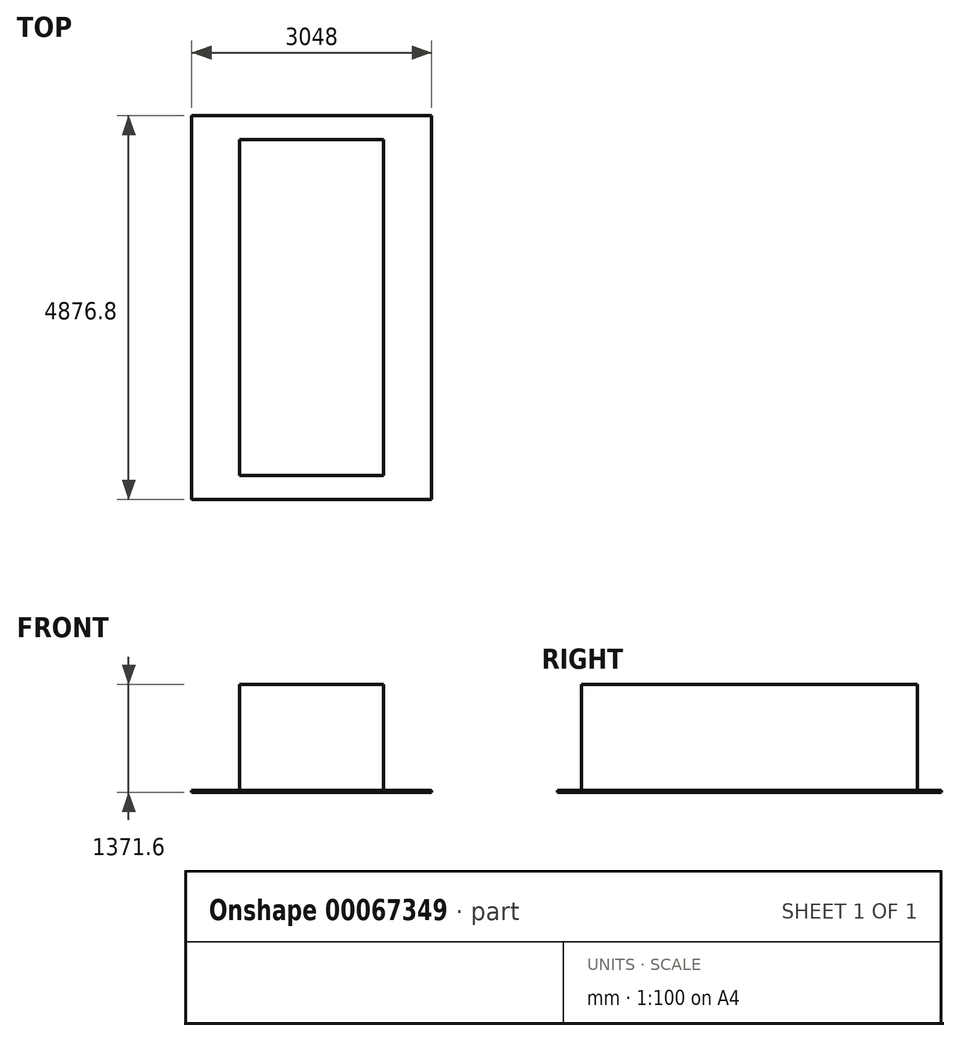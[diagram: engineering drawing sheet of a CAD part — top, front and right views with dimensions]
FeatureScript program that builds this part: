
annotation { "Feature Type Name" : "Feature", "Feature Type Description" : "" }
export const myFeature = defineFeature(function(context is Context, id is Id, definition is map)
    precondition{}
    {
        {
            var Q0;
            Q0=qCreatedBy(makeId("Top.planeOp"),FACE);
            var sketch = newSketch(context, id + "F0", { "sketchPlane" : qUnion([Q0])});
            skLineSegment(sketch, "E0.bottom", {"start": v(914.4, 2133.6) * mm, "end": v(-914.4, 2133.6) * mm});
            skLineSegment(sketch, "E0.top", {"start": v(914.4, -2133.6) * mm, "end": v(-914.4, -2133.6) * mm});
            skLineSegment(sketch, "E0.left", {"start": v(914.4, 2133.6) * mm, "end": v(914.4, -2133.6) * mm});
            skLineSegment(sketch, "E0.right", {"start": v(-914.4, 2133.6) * mm, "end": v(-914.4, -2133.6) * mm});
            skPoint(sketch, "E0.middle", {"position": v(0, 0) * mm});
            skLineSegment(sketch, "E1.0", {"start": v(1524, 2438.4) * mm, "end": v(-1524, 2438.4) * mm});
            skLineSegment(sketch, "E1.1", {"start": v(1524, 2438.4) * mm, "end": v(1524, -2438.4) * mm});
            skLineSegment(sketch, "E1.2", {"start": v(1524, -2438.4) * mm, "end": v(-1524, -2438.4) * mm});
            skLineSegment(sketch, "E1.3", {"start": v(-1524, 2438.4) * mm, "end": v(-1524, -2438.4) * mm});
            skLineSegment(sketch, "E2", {"start": v(0, 2438.4) * mm, "end": v(0, 2133.6) * mm, "construction": true});
            skLineSegment(sketch, "E3", {"start": v(0, -2438.4) * mm, "end": v(0, -2133.6) * mm, "construction": true});
            skSolve(sketch);
        }
        {
            var Q0;
            Q0=makeQuery(id+"F0.imprint","IMPRINT",FACE,{"disambiguationData":[TD([[makeQuery(id+"F0.imprint","IMPRINT",EDGE,{"derivedFrom":sQuery(id+"F0.wireOp",EDGE,"E0.bottom")}),1.0]])]});
            extrude(context, id + "F1", {"entities" : qUnion([Q0]), "depth" : 1371.6 * mm});
        }
        {
            var Q0;
            Q0=makeQuery(id+"F0.imprint","IMPRINT",FACE,{"disambiguationData":[TD([[makeQuery(id+"F0.imprint","IMPRINT",EDGE,{"derivedFrom":sQuery(id+"F0.wireOp",EDGE,"E0.bottom")}),-1.0]])]});
            extrude(context, id + "F2", {"entities" : qUnion([Q0]), "operationType" : NewBodyOperationType.ADD, "depth" : 25.4 * mm});
        }
    });
